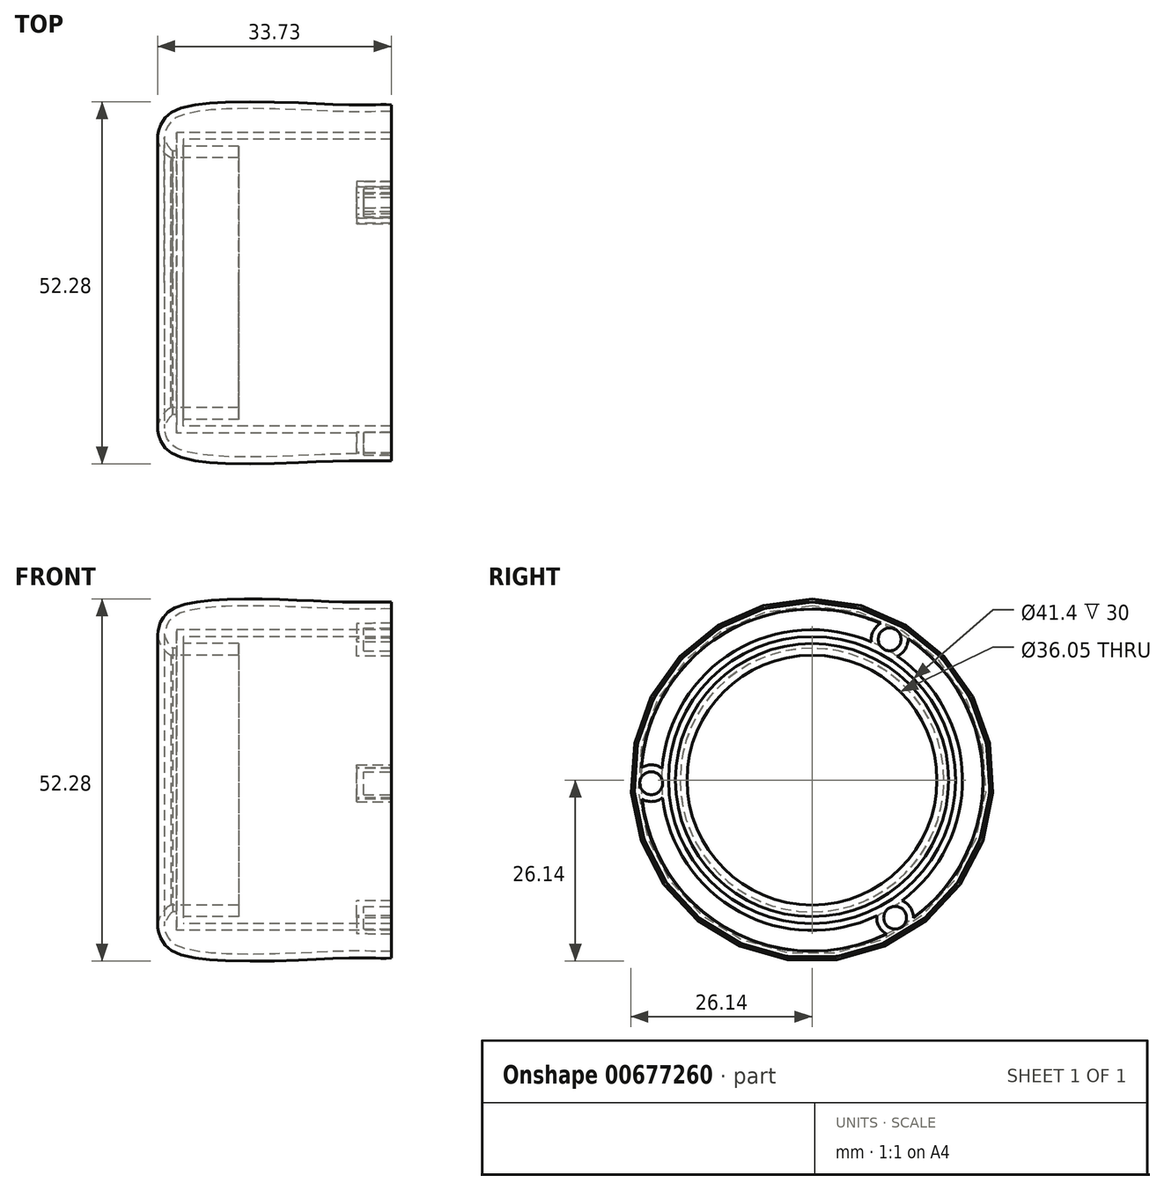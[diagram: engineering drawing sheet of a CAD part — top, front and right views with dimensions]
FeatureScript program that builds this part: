
annotation { "Feature Type Name" : "Feature", "Feature Type Description" : "" }
export const myFeature = defineFeature(function(context is Context, id is Id, definition is map)
    precondition{}
    {
        {
            var Q0;
            Q0=qCreatedBy(makeId("Front.planeOp"),FACE);
            var sketch = newSketch(context, id + "F0", { "sketchPlane" : qUnion([Q0])});
            skLineSegment(sketch, "E0", {"start": v(-49.69, 0) * mm, "end": v(63.8, 0) * mm, "construction": true});
            skLineSegment(sketch, "E1", {"start": v(-43.03, 20.7) * mm, "end": v(-13.03, 20.7) * mm});
            skLineSegment(sketch, "E2", {"start": v(-13.03, 20.7) * mm, "end": v(-13.03, 25.7) * mm});
            skLineSegment(sketch, "E3", {"start": v(-43.03, 20.7) * mm, "end": v(-43.03, 19.7) * mm});
            skLineSegment(sketch, "E4", {"start": v(-35.03, 19.7) * mm, "end": v(-43.03, 19.7) * mm});
            skLineSegment(sketch, "E5", {"start": v(-44.8, 18.02) * mm, "end": v(-35.05, 18.02) * mm});
            skLineSegment(sketch, "E6", {"start": v(-35.05, 18.02) * mm, "end": v(-35.03, 19.7) * mm});
            skFitSpline(sketch, "E7", {"points": [v(-13.03, 25.7) * mm, v(-19.91, 25.7) * mm, v(-44.25, 24.86) * mm, v(-46.62, 21.78) * mm, v(-46.64, 20.33) * mm, v(-44.8, 18.02) * mm], "startDerivative": vector(-24.83, 1) * mm, "endDerivative": vector(16.48, -5.95) * mm});
            skSolve(sketch);
        }
        {
            var Q0;
            Q0=makeQuery(id+"F0.imprint","IMPRINT",FACE,{"disambiguationData":[TD([[makeQuery(id+"F0.imprint","IMPRINT",EDGE,{"derivedFrom":sQuery(id+"F0.wireOp",EDGE,"E1")}),1.0]])]});
            var Q1;
            Q1=sQuery(id+"F0.wireOp",EDGE,"E0");
            revolve(context, id + "F1", {"entities" : qUnion([Q0]), "axis" : qUnion([Q1]), "revolveType" : RevolveType.FULL});
        }
        {
            var Q0;
            Q0=makeQuery(id+"F1.opRevolve","SWEPT_FACE",FACE,{"disambiguationData":[OSD([sQuery(id+"F0.wireOp",EDGE,"E2")])]});
            cPlane(context, id + "F2", {"entities" : qUnion([Q0]), "cplaneType" : CPlaneType.OFFSET, "offset" : 0 * mm, "width" : 150 * mm, "height" : 150 * mm});
        }
        {
            var Q0;
            Q0=qCreatedBy(id+"F2.planeOp",FACE);
            var sketch = newSketch(context, id + "F3", { "sketchPlane" : qUnion([Q0])});
            skCircle(sketch, "E8", {"center": v(-23.2, -0.45) * mm, "radius": 1.65 * mm});
            skCircle(sketch, "E9.1.0", {"center": v(11.99, -19.86) * mm, "radius": 1.65 * mm});
            skCircle(sketch, "E9.2.0", {"center": v(11.2, 20.31) * mm, "radius": 1.65 * mm});
            skPoint(sketch, "E9.center", {"position": v(0, 0) * mm});
            skSolve(sketch);
        }
        {
            var Q0;
            Q0 = qSketchRegion(id + "F3", true);
            extrude(context, id + "F4", {"entities" : qUnion([Q0]), "operationType" : NewBodyOperationType.REMOVE, "oppositeDirection" : true, "depth" : 4 * mm, "offsetDistance" : 25 * mm});
        }
        {
            var Q0;
            Q0=makeQuery(id+"F1.opRevolve","SWEPT_FACE",FACE,{"disambiguationData":[OSD([sQuery(id+"F0.wireOp",EDGE,"E2")])]});
            shell(context, id + "F5", {"entities" : qUnion([Q0]), "thickness" : 1 * mm});
        }
    });
